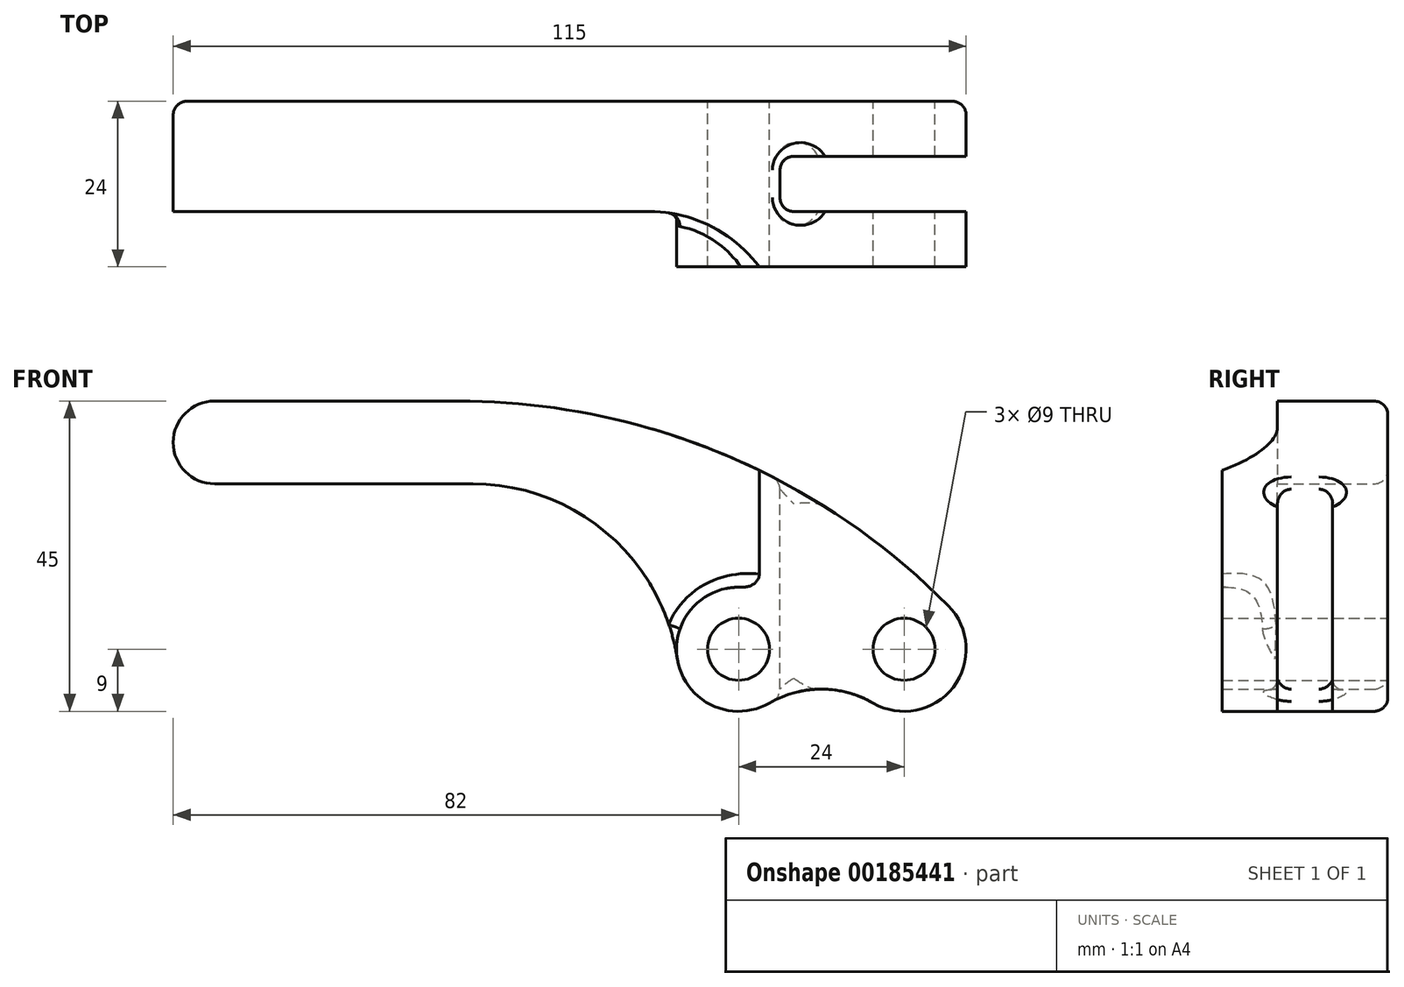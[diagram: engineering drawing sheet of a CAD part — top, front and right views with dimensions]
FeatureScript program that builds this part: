
annotation { "Feature Type Name" : "Feature", "Feature Type Description" : "" }
export const myFeature = defineFeature(function(context is Context, id is Id, definition is map)
    precondition{}
    {
        {
            var Q0;
            Q0=qCreatedBy(makeId("Front.planeOp"),FACE);
            var sketch = newSketch(context, id + "F0", { "sketchPlane" : qUnion([Q0])});
            skCircle(sketch, "E0", {"center": v(0, 0) * mm, "radius": 6 * mm});
            skCircle(sketch, "E1", {"center": v(76, -30) * mm, "radius": 9 * mm});
            skCircle(sketch, "E2", {"center": v(100, -30) * mm, "radius": 9 * mm});
            skLineSegment(sketch, "E3", {"start": v(0, 6) * mm, "end": v(35.3, 6) * mm});
            skLineSegment(sketch, "E4", {"start": v(0, -6) * mm, "end": v(37.46, -6) * mm});
            skArc(sketch, "E5", {"start": v(37.46, -6) * mm, "mid": v(56.98, -13.21) * mm, "end": v(67.1, -31.38) * mm});
            skArc(sketch, "E6", {"start": v(35.3, 6) * mm, "mid": v(73.82, -1.72) * mm, "end": v(106.4, -23.67) * mm});
            skArc(sketch, "E7", {"start": v(95.5, -37.8) * mm, "mid": v(88, -35.78) * mm, "end": v(80.5, -37.8) * mm});
            skCircle(sketch, "E8", {"center": v(76, -30) * mm, "radius": 4.5 * mm});
            skCircle(sketch, "E9", {"center": v(100, -30) * mm, "radius": 4.5 * mm});
            skSolve(sketch);
        }
        {
            var Q0;
            Q0 = qSketchRegion(id + "F0", true);
            extrude(context, id + "F1", {"entities" : qUnion([Q0]), "depth" : 24 * mm, "symmetric" : true});
        }
        {
            var Q0;
            Q0=makeQuery(id+"F1.opExtrude","SWEPT_FACE",FACE,{"disambiguationData":[OSD([sQuery(id+"F0.wireOp",EDGE,"E3")])]});
            var sketch = newSketch(context, id + "F2", { "sketchPlane" : qUnion([Q0])});
            skLineSegment(sketch, "E10", {"start": v(-15.68, -4) * mm, "end": v(63, -4) * mm});
            skArc(sketch, "E11", {"start": v(63, -4) * mm, "mid": v(71.94, -6.11) * mm, "end": v(79, -12) * mm});
            skLineSegment(sketch, "E12", {"start": v(-6, -12) * mm, "end": v(-6, 12) * mm});
            skLineSegment(sketch, "E13.0", {"start": v(0, -12) * mm, "end": v(35.3, -12) * mm});
            skLineSegment(sketch, "E14.0", {"start": v(35.3, -12) * mm, "end": v(106.4, -12) * mm});
            skPoint(sketch, "E15", {"position": v(70.85, -12) * mm});
            skLineSegment(sketch, "E16.0", {"start": v(0, -12) * mm, "end": v(-6, -12) * mm});
            skSolve(sketch);
        }
        {
            var Q0;
            Q0 = qSketchRegion(id + "F2", true);
            extrude(context, id + "F3", {"entities" : qUnion([Q0]), "operationType" : NewBodyOperationType.REMOVE, "endBound" : BoundingType.THROUGH_ALL, "oppositeDirection" : true, "depth" : 25 * mm});
        }
        {
            var Q0;
            Q0=qCreatedBy(makeId("Front.planeOp"),FACE);
            var sketch = newSketch(context, id + "F4", { "sketchPlane" : qUnion([Q0])});
            skCircle(sketch, "E17.0", {"center": v(76, -30) * mm, "radius": 9 * mm});
            skCircle(sketch, "E18.0", {"center": v(76, -30) * mm, "radius": 4.5 * mm});
            skSolve(sketch);
        }
        {
            var Q0;
            Q0 = qSketchRegion(id + "F4", true);
            extrude(context, id + "F5", {"entities" : qUnion([Q0]), "operationType" : NewBodyOperationType.ADD, "depth" : 24 * mm, "symmetric" : true});
        }
        {
            var Q0;
            Q0=makeQuery(id+"F1.opExtrude","SWEPT_FACE",FACE,{"disambiguationData":[OSD([sQuery(id+"F0.wireOp",EDGE,"E3")])]});
            var sketch = newSketch(context, id + "F6", { "sketchPlane" : qUnion([Q0])});
            skLineSegment(sketch, "E19.bottom", {"start": v(82, 4) * mm, "end": v(109, 4) * mm});
            skLineSegment(sketch, "E19.top", {"start": v(82, -4) * mm, "end": v(109, -4) * mm});
            skLineSegment(sketch, "E19.left", {"start": v(82, 4) * mm, "end": v(82, -4) * mm});
            skLineSegment(sketch, "E19.right", {"start": v(109, 4) * mm, "end": v(109, -4) * mm});
            skPoint(sketch, "E19.middle", {"position": v(95.5, 0) * mm});
            skLineSegment(sketch, "E20.0", {"start": v(104.5, -12) * mm, "end": v(95.5, -12) * mm});
            skPoint(sketch, "E21", {"position": v(100, -12) * mm});
            skLineSegment(sketch, "E22", {"start": v(109, 12) * mm, "end": v(109, -12) * mm});
            skSolve(sketch);
        }
        {
            var Q0;
            Q0 = qSketchRegion(id + "F6", true);
            extrude(context, id + "F7", {"entities" : qUnion([Q0]), "operationType" : NewBodyOperationType.REMOVE, "endBound" : BoundingType.THROUGH_ALL, "oppositeDirection" : true, "depth" : 25 * mm});
        }
        {
            var Q0;
            Q0=makeQuery(id+"F3.boolean.opBoolean","COPY",EDGE,{"derivedFrom":makeQuery(id+"F3.opExtrude","CAP_EDGE",EDGE,{"disambiguationData":[OSD([sQuery(id+"F2.wireOp",EDGE,"E10")])],"isStart":true})});
            var Q1;
            Q1=makeQuery(id+"FklrVE2HTrgASQ2_1.1.F3.boolean.opBoolean","COPY",EDGE,{"derivedFrom":makeQuery(id+"FklrVE2HTrgASQ2_1.1.F3.opExtrude","CAP_EDGE",EDGE,{"disambiguationData":[OSD([sQuery(id+"F2.wireOp",EDGE,"E10")])],"isStart":true})});
            var Q2;
            Q2=makeQuery(id+"F5.boolean.opBoolean","INTERSECT",EDGE,{"derivedFrom":[makeQuery(id+"F3.boolean.opBoolean","COPY",FACE,{"derivedFrom":makeQuery(id+"F3.opExtrude","SWEPT_FACE",FACE,{"disambiguationData":[OSD([sQuery(id+"F2.wireOp",EDGE,"E11")])]})}),makeQuery(id+"F5.opExtrude","SWEPT_FACE",FACE,{"disambiguationData":[OSD([sQuery(id+"F4.wireOp",EDGE,"E17.0")])]})]});
            var Q3;
            {var subQ1=sQuery(id+"F0.wireOp",EDGE,"E6");var subQ2=sQuery(id+"F2.wireOp",EDGE,"E11");Q3=makeQuery(id+"F3.boolean.opBoolean","COPY",EDGE,{"disambiguationData":[TD([makeQuery(id+"F1.opExtrude","SWEPT_FACE",FACE,{"disambiguationData":[OSD([subQ1])]})])],"derivedFrom":makeQuery(id+"F3.opExtrude","SWEPT_EDGE",EDGE,{"disambiguationData":[OSD([subQ2,sQuery(id+"F2.wireOp",EDGE,"E14.0")])]})});}
            var Q4;
            Q4=makeQuery(id+"F1.opExtrude","CAP_EDGE",EDGE,{"disambiguationData":[OSD([sQuery(id+"F0.wireOp",EDGE,"E6")])],"isStart":true});
            var Q5;
            Q5=makeQuery(id+"F5.boolean.opBoolean","INTERSECT",EDGE,{"derivedFrom":[makeQuery(id+"FklrVE2HTrgASQ2_1.1.F3.boolean.opBoolean","COPY",FACE,{"derivedFrom":makeQuery(id+"FklrVE2HTrgASQ2_1.1.F3.opExtrude","SWEPT_FACE",FACE,{"disambiguationData":[OSD([sQuery(id+"F2.wireOp",EDGE,"E11")])]})}),makeQuery(id+"F5.opExtrude","SWEPT_FACE",FACE,{"disambiguationData":[OSD([sQuery(id+"F4.wireOp",EDGE,"E17.0")])]})]});
            var Q6;
            Q6=makeQuery(id+"F7.boolean.opBoolean","COPY",FACE,{"derivedFrom":makeQuery(id+"F7.opExtrude","SWEPT_FACE",FACE,{"disambiguationData":[OSD([sQuery(id+"F6.wireOp",EDGE,"E19.left")])]})});
            fillet(context, id + "F8", {"entities" : qUnion([Q0, Q1, Q2, Q3, Q4, Q5, Q6]), "radius" : 2 * mm, "tangentPropagation" : true, "allowEdgeOverflow" : false});
        }
    });
